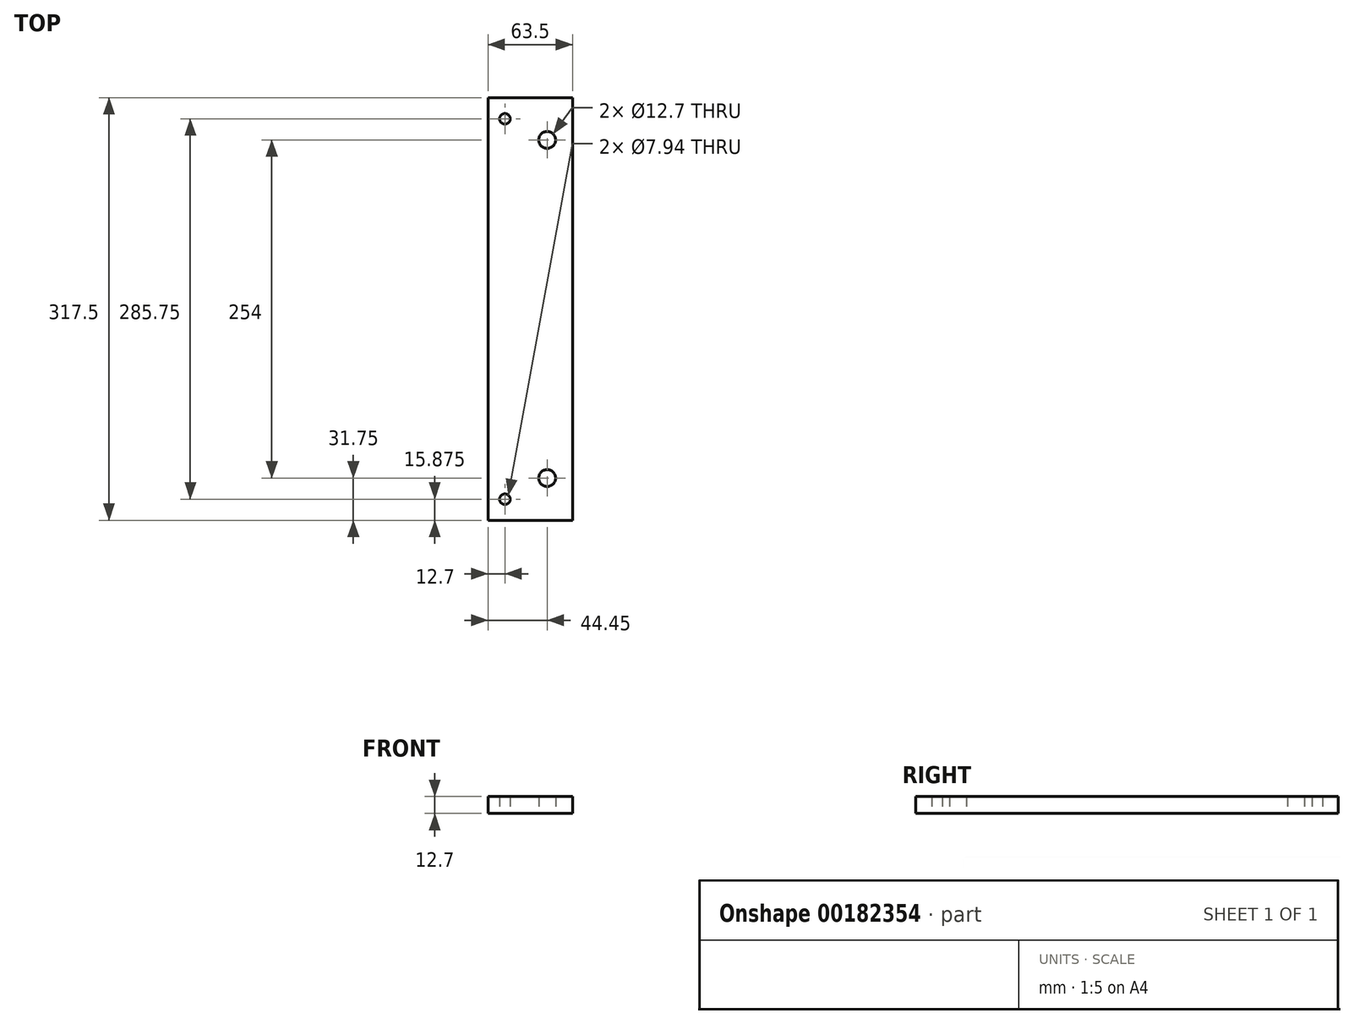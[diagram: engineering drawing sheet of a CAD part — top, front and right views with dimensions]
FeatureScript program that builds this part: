
annotation { "Feature Type Name" : "Feature", "Feature Type Description" : "" }
export const myFeature = defineFeature(function(context is Context, id is Id, definition is map)
    precondition{}
    {
        {
            var Q0;
            Q0=qCreatedBy(makeId("Top.planeOp"),FACE);
            var sketch = newSketch(context, id + "F0", { "sketchPlane" : qUnion([Q0])});
            skLineSegment(sketch, "E0.bottom", {"start": v(-86.52, 158.75) * mm, "end": v(-23.02, 158.75) * mm});
            skLineSegment(sketch, "E0.top", {"start": v(-86.52, -158.75) * mm, "end": v(-23.02, -158.75) * mm});
            skLineSegment(sketch, "E0.left", {"start": v(-86.52, 158.75) * mm, "end": v(-86.52, -158.75) * mm});
            skLineSegment(sketch, "E0.right", {"start": v(-23.02, 158.75) * mm, "end": v(-23.02, -158.75) * mm});
            skCircle(sketch, "E1", {"center": v(-42.07, 127) * mm, "radius": 6.35 * mm});
            skCircle(sketch, "E2", {"center": v(-42.07, -127) * mm, "radius": 6.35 * mm});
            skPoint(sketch, "E3", {"position": v(-86.52, 0) * mm});
            skCircle(sketch, "E4", {"center": v(-73.82, 142.88) * mm, "radius": 3.97 * mm});
            skCircle(sketch, "E5", {"center": v(-73.82, -142.88) * mm, "radius": 3.97 * mm});
            skLineSegment(sketch, "E6", {"start": v(-58.07, -158.75) * mm, "end": v(-58.07, -104.13) * mm});
            skSolve(sketch);
        }
        {
            var Q0;
            Q0 = qSketchRegion(id + "F0", true);
            extrude(context, id + "F1", {"entities" : qUnion([Q0]), "depth" : 12.7 * mm});
        }
    });
